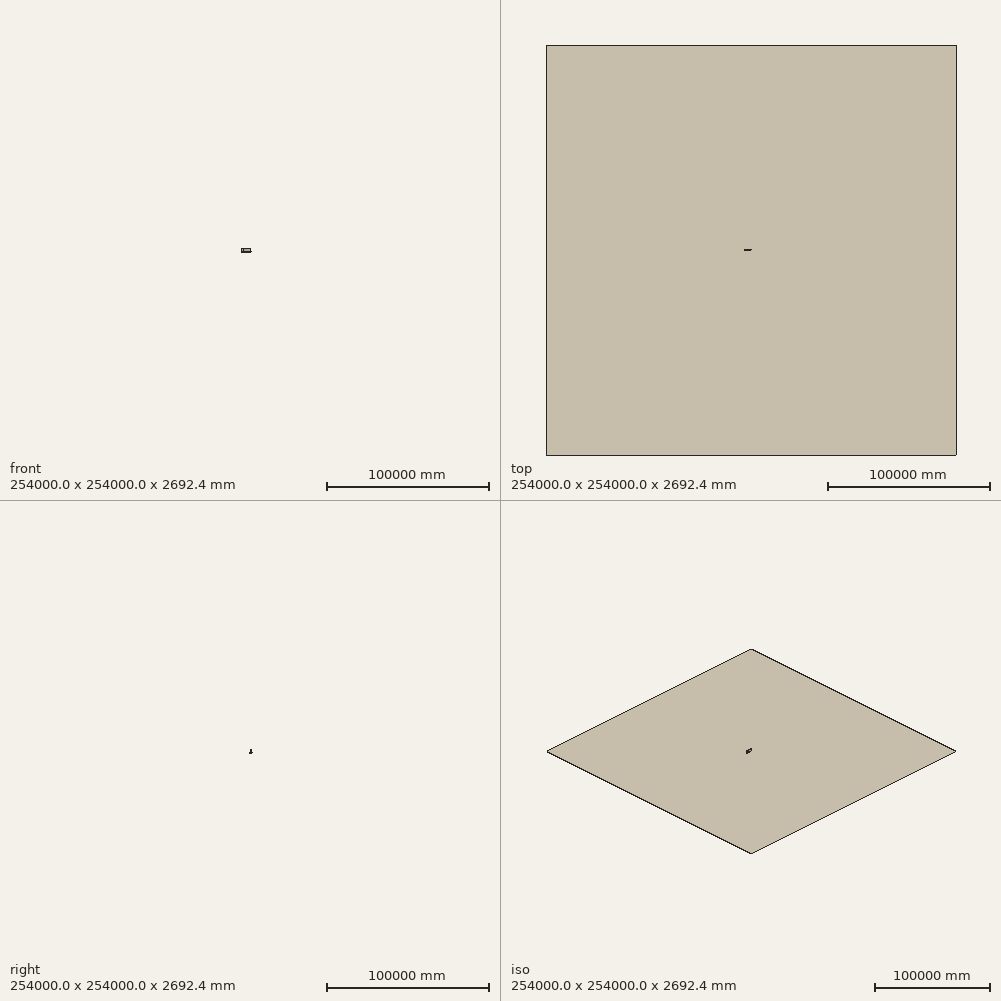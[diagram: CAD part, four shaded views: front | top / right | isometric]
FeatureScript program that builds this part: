
annotation { "Feature Type Name" : "Feature", "Feature Type Description" : "" }
export const myFeature = defineFeature(function(context is Context, id is Id, definition is map)
    precondition{}
    {
        {
            var Q0;
            Q0=qCreatedBy(makeId("Top.planeOp"),FACE);
            var sketch = newSketch(context, id + "F0", { "sketchPlane" : qUnion([Q0])});
            skLineSegment(sketch, "E0", {"start": v(-152.4, 0) * mm, "end": v(366.8, 0) * mm, "construction": true});
            skLineSegment(sketch, "E1", {"start": v(-152.4, 0) * mm, "end": v(-152.4, -152.4) * mm});
            skArc(sketch, "E2", {"start": v(-152.4, -152.4) * mm, "mid": v(1943.1, -457.2) * mm, "end": v(4038.6, -152.4) * mm});
            skCircle(sketch, "E3", {"center": v(1943.1, -457.2) * mm, "radius": 10.16 * mm, "construction": true});
            skLineSegment(sketch, "E4.MirrorCS", {"start": v(-152.4, 0) * mm, "end": v(-152.4, 152.4) * mm});
            skArc(sketch, "E5.MirrorCS", {"start": v(-152.4, 152.4) * mm, "mid": v(1943.1, 457.2) * mm, "end": v(4038.6, 152.4) * mm});
            skPoint(sketch, "E6.endSnap0", {"position": v(-152.4, -76.2) * mm});
            skPoint(sketch, "E7.oppositeSnap0", {"position": v(-212.23, 0) * mm});
            skLineSegment(sketch, "E8", {"start": v(0, -163.45) * mm, "end": v(0, 185.23) * mm, "construction": true});
            skLineSegment(sketch, "E9", {"start": v(4038.6, 152.4) * mm, "end": v(4038.6, -152.4) * mm});
            skSolve(sketch);
        }
        {
            var Q0;
            Q0=makeQuery(id+"F0.imprint","IMPRINT",FACE,{"disambiguationData":[TD([[makeQuery(id+"F0.imprint","IMPRINT",EDGE,{"derivedFrom":sQuery(id+"F0.wireOp",EDGE,"20d4d174-ac9f-4229-bbe2-37e8f4ade8900.MirrorCS")}),-1.0]])]});
            var Q1;
            Q1=makeQuery(id+"F0.imprint","IMPRINT",FACE,{"disambiguationData":[TD([[makeQuery(id+"F0.imprint","IMPRINT",EDGE,{"derivedFrom":sQuery(id+"F0.wireOp",EDGE,"E1")}),1.0]])]});
            extrude(context, id + "F1", {"entities" : qUnion([Q0, Q1]), "endBound" : BoundingType.SYMMETRIC, "depth" : 1676.4 * mm, "offsetDistance" : 25.4 * mm});
        }
        {
            var Q0;
            Q0=qCreatedBy(makeId("Front.planeOp"),FACE);
            var sketch = newSketch(context, id + "F2", { "sketchPlane" : qUnion([Q0])});
            skLineSegment(sketch, "E10", {"start": v(-228.6, 0) * mm, "end": v(-228.6, 838.2) * mm});
            skLineSegment(sketch, "E11", {"start": v(-228.6, 838.2) * mm, "end": v(-1447.8, 838.2) * mm});
            skLineSegment(sketch, "E12", {"start": v(-1447.8, 838.2) * mm, "end": v(-1447.8, -1549.4) * mm});
            skLineSegment(sketch, "E13", {"start": v(-1447.8, -1549.4) * mm, "end": v(4038.6, -1549.4) * mm});
            skLineSegment(sketch, "E14", {"start": v(4038.6, -1549.4) * mm, "end": v(4038.6, -939.8) * mm});
            skLineSegment(sketch, "E15", {"start": v(4038.6, -939.8) * mm, "end": v(-228.6, -939.8) * mm});
            skLineSegment(sketch, "E16", {"start": v(-228.6, -939.8) * mm, "end": v(-228.6, 0) * mm});
            skSolve(sketch);
        }
        {
            var Q0;
            Q0=makeQuery(id+"F2.imprint","IMPRINT",FACE,{"disambiguationData":[TD([[makeQuery(id+"F2.imprint","IMPRINT",EDGE,{"derivedFrom":sQuery(id+"F2.wireOp",EDGE,"E10")}),1.0]])]});
            extrude(context, id + "F3", {"entities" : qUnion([Q0]), "endBound" : BoundingType.SYMMETRIC, "depth" : 304.8 * mm, "offsetDistance" : 25.4 * mm});
        }
        {
            var Q0;
            Q0=makeQuery(id+"F3.opExtrude","SWEPT_FACE",FACE,{"disambiguationData":[OSD([sQuery(id+"F2.wireOp",EDGE,"E13")])]});
            var sketch = newSketch(context, id + "F4", { "sketchPlane" : qUnion([Q0])});
            skLineSegment(sketch, "E17.bottom", {"start": v(-1564.85, 868.75) * mm, "end": v(4453.84, 868.75) * mm});
            skLineSegment(sketch, "E17.top", {"start": v(-1564.85, -849.25) * mm, "end": v(4453.84, -849.25) * mm});
            skLineSegment(sketch, "E17.left", {"start": v(-1564.85, 868.75) * mm, "end": v(-1564.85, -849.25) * mm});
            skLineSegment(sketch, "E17.right", {"start": v(4453.84, 868.75) * mm, "end": v(4453.84, -849.25) * mm});
            skLineSegment(sketch, "E18.0", {"start": v(-1666.45, 970.35) * mm, "end": v(4555.44, 970.35) * mm});
            skLineSegment(sketch, "E18.1", {"start": v(-1666.45, 970.35) * mm, "end": v(-1666.45, -950.85) * mm});
            skLineSegment(sketch, "E18.2", {"start": v(-1666.45, -950.85) * mm, "end": v(4555.44, -950.85) * mm});
            skLineSegment(sketch, "E18.3", {"start": v(4555.44, 970.35) * mm, "end": v(4555.44, -950.85) * mm});
            skSolve(sketch);
        }
        {
            var Q0;
            Q0=makeQuery(id+"F4.imprint","IMPRINT",FACE,{"disambiguationData":[TD([[makeQuery(id+"F4.imprint","IMPRINT",EDGE,{"derivedFrom":sQuery(id+"F4.wireOp",EDGE,"E17.bottom")}),1.0]])]});
            extrude(context, id + "F5", {"entities" : qUnion([Q0]), "endBound" : BoundingType.SYMMETRIC, "depth" : 254 * mm, "offsetDistance" : 25.4 * mm});
        }
        {
            var Q0;
            Q0=makeQuery(id+"F3.opExtrude","SWEPT_FACE",FACE,{"disambiguationData":[OSD([sQuery(id+"F2.wireOp",EDGE,"E13")])]});
            var sketch = newSketch(context, id + "F6", { "sketchPlane" : qUnion([Q0])});
            skLineSegment(sketch, "E19.bottom", {"start": v(-122961.4, -126847.6) * mm, "end": v(131038.6, -126847.6) * mm});
            skLineSegment(sketch, "E19.top", {"start": v(-122961.4, 127152.4) * mm, "end": v(131038.6, 127152.4) * mm});
            skLineSegment(sketch, "E19.left", {"start": v(-122961.4, -126847.6) * mm, "end": v(-122961.4, 127152.4) * mm});
            skLineSegment(sketch, "E19.right", {"start": v(131038.6, -126847.6) * mm, "end": v(131038.6, 127152.4) * mm});
            skSolve(sketch);
        }
        {
            var Q0;
            Q0=makeQuery(id+"F6.imprint","IMPRINT",FACE,{"disambiguationData":[TD([[makeQuery(id+"F6.imprint","IMPRINT",EDGE,{"derivedFrom":sQuery(id+"F6.wireOp",EDGE,"E19.bottom")}),1.0]])]});
            extrude(context, id + "F7", {"entities" : qUnion([Q0]), "depth" : 304.8 * mm, "offsetDistance" : 25.4 * mm});
        }
    });
